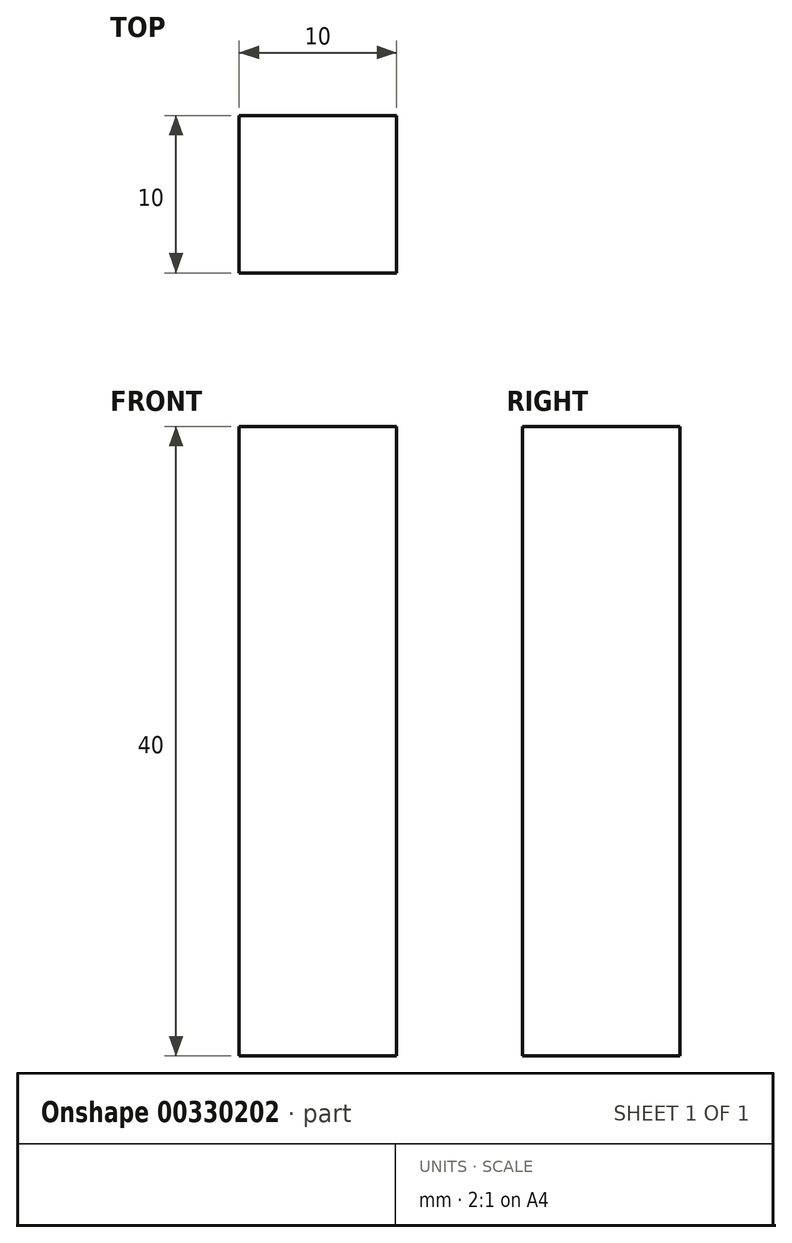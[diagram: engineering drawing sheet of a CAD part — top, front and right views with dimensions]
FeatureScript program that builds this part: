
annotation { "Feature Type Name" : "Feature", "Feature Type Description" : "" }
export const myFeature = defineFeature(function(context is Context, id is Id, definition is map)
    precondition{}
    {
        {
            var Q0;
            Q0=qCreatedBy(makeId("Front.planeOp"),FACE);
            var sketch = newSketch(context, id + "F0", { "sketchPlane" : qUnion([Q0])});
            skLineSegment(sketch, "E0.bottom", {"start": v(-3.38, 32.7) * mm, "end": v(6.62, 32.7) * mm});
            skLineSegment(sketch, "E0.top", {"start": v(-3.38, -7.3) * mm, "end": v(6.62, -7.3) * mm});
            skLineSegment(sketch, "E0.left", {"start": v(-3.38, 32.7) * mm, "end": v(-3.38, -7.3) * mm});
            skLineSegment(sketch, "E0.right", {"start": v(6.62, 32.7) * mm, "end": v(6.62, -7.3) * mm});
            skSolve(sketch);
        }
        {
            var Q0;
            Q0=makeQuery(id+"F0.imprint","IMPRINT",FACE,{"disambiguationData":[TD([[makeQuery(id+"F0.imprint","IMPRINT",EDGE,{"derivedFrom":sQuery(id+"F0.wireOp",EDGE,"E0.bottom")}),-1.0]])]});
            extrude(context, id + "F1", {"entities" : qUnion([Q0]), "depth" : 10 * mm});
        }
    });
